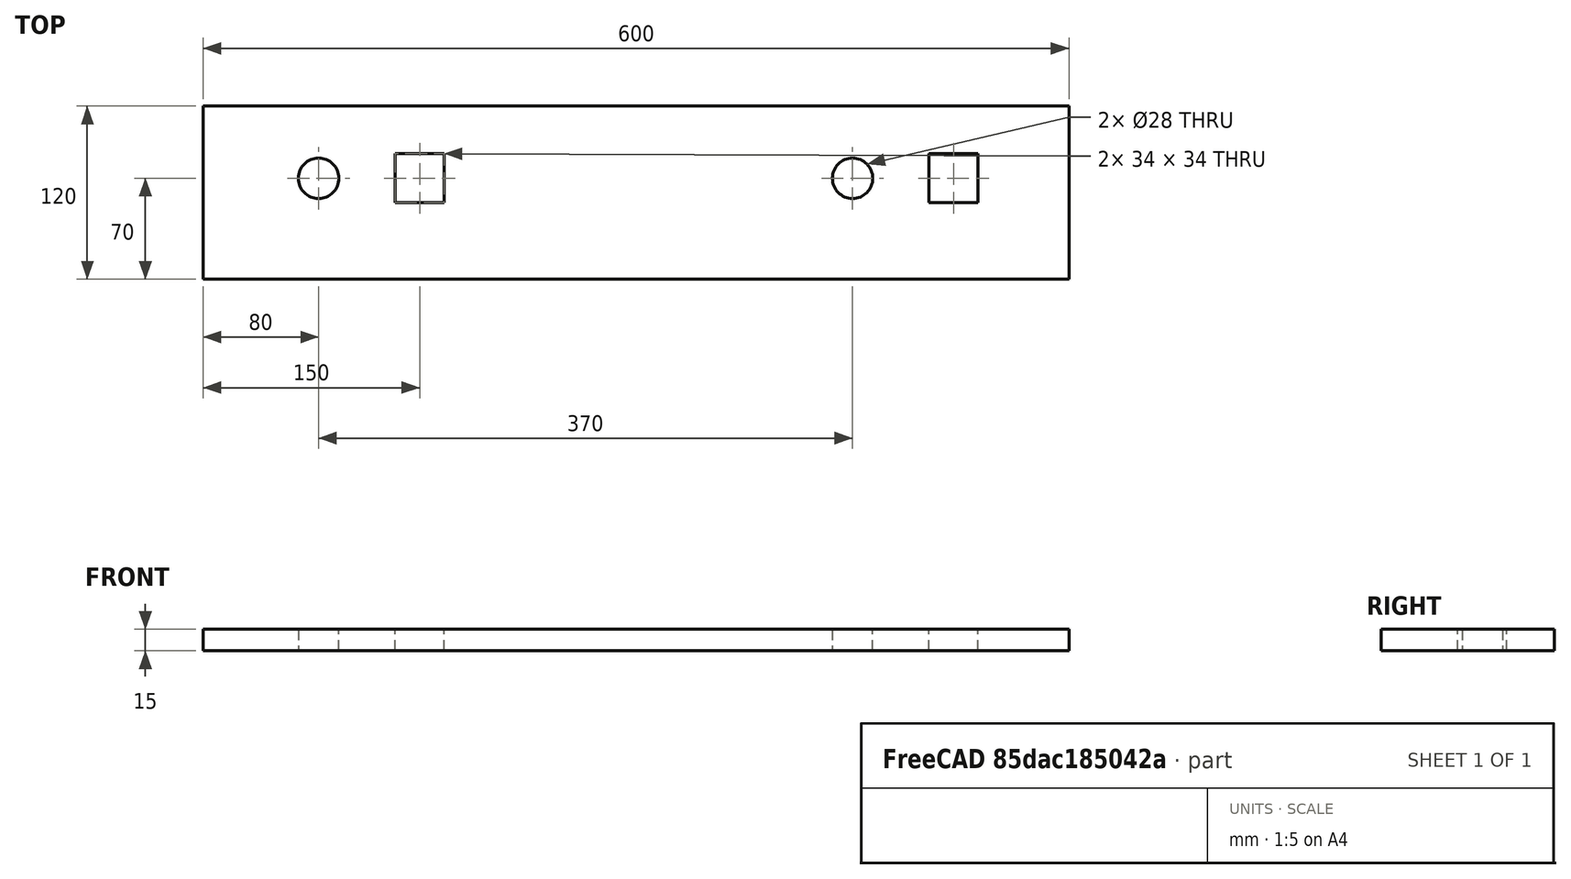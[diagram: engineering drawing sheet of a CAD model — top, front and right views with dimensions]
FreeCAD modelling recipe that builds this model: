
FCSTD DOCUMENT  (FreeCAD 1.0R39319 (Git))
Label: ctrl_panel_front
License: All rights reserved
LicenseURL: http://en.wikipedia.org/wiki/All_rights_reserved
objects: Sketcher::SketchObject×1, PartDesign::Pad×1, PartDesign::Body×1
note: 6 computed .brp shape members not serialized (recipe doc carries the construction recipe); baked Part::Feature solids carry a one-line shape summary decoded from their .brp

FEATURE [Sketcher::SketchObject] Sketch  label="ctrl_panel_front_sketch"
  ArcFitTolerance = 0
  AttachmentSupport = -> [XY_Plane]
  FullyConstrained = true
  MakeInternals = false
  MapMode = 5
  sketch-geometry (23):
    g0: LineSegment StartX=0 StartY=0 StartZ=0 EndX=600 EndY=0 EndZ=0
    g1: LineSegment StartX=600 StartY=0 StartZ=0 EndX=600 EndY=120 EndZ=0
    g2: LineSegment StartX=600 StartY=120 StartZ=0 EndX=0 EndY=120 EndZ=0
    g3: LineSegment StartX=0 StartY=120 StartZ=0 EndX=0 EndY=0 EndZ=0
    g4: Circle CenterX=80 CenterY=70 CenterZ=0 NormalX=0 NormalY=0 NormalZ=1 AngleXU=0 Radius=14
    g5: Circle CenterX=450 CenterY=70 CenterZ=0 NormalX=0 NormalY=0 NormalZ=1 AngleXU=0 Radius=14
    g6: LineSegment [constr] StartX=80 StartY=70 StartZ=0 EndX=0 EndY=70 EndZ=0
    g7: LineSegment [constr] StartX=80 StartY=70 StartZ=0 EndX=80 EndY=120 EndZ=0
    g8: LineSegment [constr] StartX=450 StartY=70 StartZ=0 EndX=450 EndY=120 EndZ=0
    g9: LineSegment StartX=133 StartY=87 StartZ=0 EndX=133 EndY=53 EndZ=0
    g10: LineSegment StartX=133 StartY=53 StartZ=0 EndX=167 EndY=53 EndZ=0
    g11: LineSegment StartX=167 StartY=53 StartZ=0 EndX=167 EndY=87 EndZ=0
    g12: LineSegment StartX=167 StartY=87 StartZ=0 EndX=133 EndY=87 EndZ=0
    g13: LineSegment [constr] StartX=133 StartY=87 StartZ=0 EndX=167 EndY=53 EndZ=0
    g14: LineSegment [constr] StartX=167 StartY=87 StartZ=0 EndX=133 EndY=53 EndZ=0
    g15: GeomPoint [constr] X=150 Y=70 Z=0
    g16: LineSegment StartX=503 StartY=87 StartZ=0 EndX=503 EndY=53 EndZ=0
    g17: LineSegment StartX=503 StartY=53 StartZ=0 EndX=537 EndY=53 EndZ=0
    g18: LineSegment StartX=537 StartY=53 StartZ=0 EndX=537 EndY=87 EndZ=0
    g19: LineSegment StartX=537 StartY=87 StartZ=0 EndX=503 EndY=87 EndZ=0
    g20: LineSegment [constr] StartX=503 StartY=53 StartZ=0 EndX=537 EndY=87 EndZ=0
    g21: LineSegment [constr] StartX=537 StartY=53 StartZ=0 EndX=503 EndY=87 EndZ=0
    g22: GeomPoint [constr] X=520 Y=70 Z=0
  constraints (62):
    c: Coincident(g0,g1)
    c: Coincident(g1,g2)
    c: Coincident(g2,g3)
    c: Coincident(g3,g0)
    c: Horizontal(g0)
    c: Horizontal(g2)
    c: Vertical(g1)
    c: Vertical(g3)
    c: Coincident(g0,g-1)
    c: DistanceX(g0,g0) = 600
    c: DistanceY(g3,g3) = 120
    c: Coincident(g6,g4)
    c: PointOnObject(g6,g3)
    c: Horizontal(g6)
    c: PointOnObject(g7,g2)
    c: Vertical(g7)
    c: Coincident(g8,g5)
    c: PointOnObject(g8,g2)
    c: Vertical(g8)
    c: Equal(g8,g7)
    c: DistanceY(g7,g7) = 50
    c: Coincident(g7,g4)
    c: DistanceX(g6,g6) = 80
    c: DistanceX(g5,g1) = 150
    c: Diameter(g4) = 28
    c: Equal(g5,g4)
    c: Coincident(g9,g10)
    c: Coincident(g10,g11)
    c: Coincident(g11,g12)
    c: Coincident(g12,g9)
    c: Vertical(g9)
    c: Vertical(g11)
    c: Horizontal(g10)
    c: Horizontal(g12)
    c: Equal(g10,g11)
    c: DistanceX(g12,g12) = 34
    c: Coincident(g13,g9)
    c: Coincident(g13,g10)
    c: Coincident(g14,g11)
    c: Coincident(g14,g9)
    c: PointOnObject(g15,g14)
    c: PointOnObject(g15,g13)
    c: DistanceX(g2,g15) = 150
    c: PointOnObject(g15,g6)
    c: Coincident(g16,g17)
    c: Coincident(g17,g18)
    c: Coincident(g18,g19)
    c: Coincident(g19,g16)
    c: Vertical(g16)
    c: Vertical(g18)
    c: Horizontal(g17)
    c: Horizontal(g19)
    c: Equal(g17,g16)
    c: Equal(g16,g11)
    c: PointOnObject(g16,g12)
    c: Coincident(g20,g16)
    c: Coincident(g20,g18)
    c: Coincident(g21,g17)
    c: Coincident(g21,g16)
    c: PointOnObject(g22,g20)
    c: PointOnObject(g22,g21)
    c: DistanceX(g22,g1) = 80
FEATURE [PartDesign::Pad] Pad  label="ctrl_panel_pad"
  AllowMultiFace = false
  Direction = (0,0,1)
  Length = 15
  Length2 = 100
  Profile = -> Sketch
  ReferenceAxis = -> Sketch [N_Axis]
  Suppressed = false
  Type = 0
FEATURE [PartDesign::Body] Body  label="ctrl_panel_body"
  AllowCompound = false
  Group = -> [Sketch,Pad]
  Origin = -> Origin
  Tip = -> Pad
